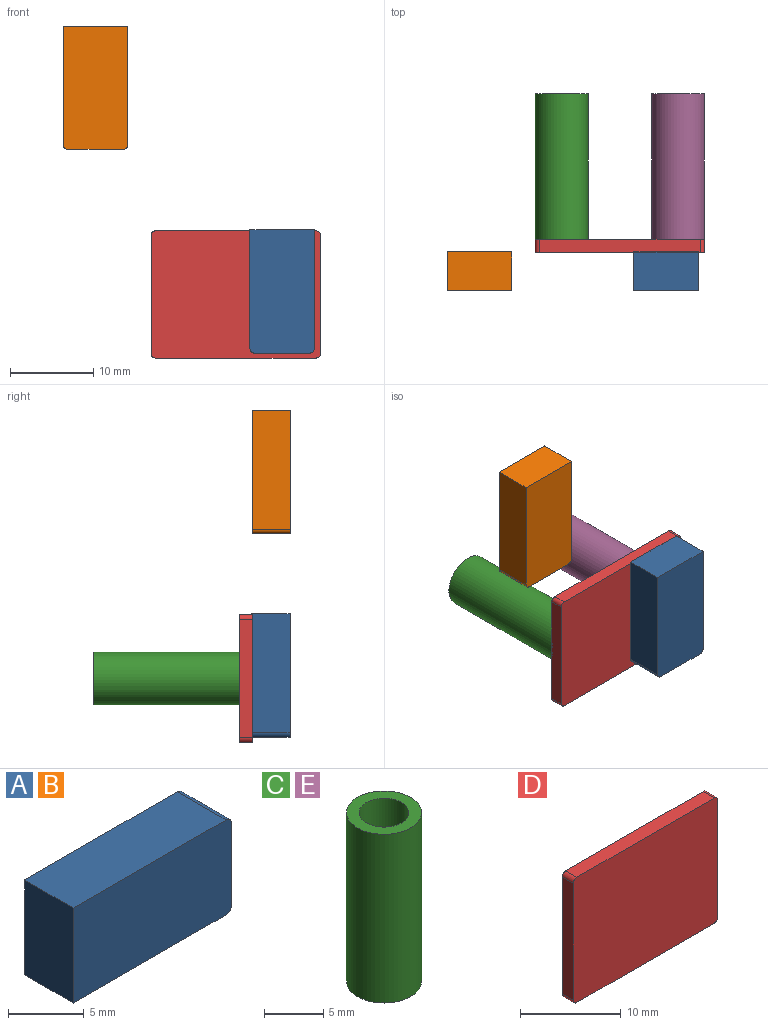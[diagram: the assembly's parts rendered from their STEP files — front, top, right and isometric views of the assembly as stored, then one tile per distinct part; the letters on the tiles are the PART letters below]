
ASSEMBLY  parts=5 mates=3
PART A: 8 faces, bbox 14.8x4.6x7.7 mm
  f0: plane 14.3x4.57mm, normal (0,0,1), area 65.4mm2, adj f1,f4,f5,f6
  f1: plane 7.7x4.57mm, normal (-1,0,0), area 35.2mm2, adj f0,f2,f4,f5
  f2: plane 14.3x4.57mm, normal (0,0,-1), area 65.4mm2, adj f1,f4,f5,f7
  f3: plane 6.68x4.57mm, normal (1,0,0), area 30.5mm2, adj f4,f5,f6,f7
  f4: plane 14.81x7.7mm, normal (0,-1,0), area 113.9mm2, adj f0,f1,f2,f3,f6,f7
  f5: plane 14.81x7.7mm, normal (0,1,0), area 113.9mm2, adj f0,f1,f2,f3,f6,f7
  f6: cylinder r=0.51mm len=4.57mm, axis (0,1,0), area 3.6mm2, adj f0,f3,f4,f5
  f7: cylinder r=0.51mm len=4.57mm, axis (0,-1,0), area 3.6mm2, adj f2,f3,f4,f5
PART B: same geometry as A
PART C: 4 faces, bbox 6.4x6.4x17.5 mm
  f0: cylinder r=2.11mm len=17.46mm, axis (0,0,-1), area 231.3mm2, adj f2,f3
  f1: cylinder r=3.17mm len=17.46mm, axis (0,0,-1), area 348.4mm2, adj f2,f3
  f2: plane 6.35x6.35mm, normal (0,0,1), area 17.7mm2, adj f0,f1
  f3: plane 6.35x6.35mm, normal (0,0,-1), area 17.7mm2, adj f0,f1
PART D: 10 faces, bbox 20.3x1.6x15.2 mm
  f0: plane 14.22x1.57mm, normal (1,0,0), area 22.4mm2, adj f4,f5,f6,f9
  f1: plane 19.3x1.57mm, normal (0,0,1), area 30.4mm2, adj f4,f5,f6,f7
  f2: plane 14.22x1.57mm, normal (-1,0,0), area 22.4mm2, adj f4,f5,f7,f8
  f3: plane 19.3x1.57mm, normal (0,0,-1), area 30.4mm2, adj f4,f5,f8,f9
  f4: plane 20.32x15.24mm, normal (0,-1,0), area 309.5mm2, adj f0,f1,f2,f3,f6,f7,f8,f9
  f5: plane 20.32x15.24mm, normal (0,1,0), area 309.5mm2, adj f0,f1,f2,f3,f6,f7,f8,f9
  f6: cylinder r=0.51mm len=1.57mm, axis (0,-1,0), area 1.3mm2, adj f0,f1,f4,f5
  f7: cylinder r=0.51mm len=1.57mm, axis (0,1,0), area 1.3mm2, adj f1,f2,f4,f5
  f8: cylinder r=0.51mm len=1.57mm, axis (0,-1,0), area 1.3mm2, adj f2,f3,f4,f5
  f9: cylinder r=0.51mm len=1.57mm, axis (0,1,0), area 1.3mm2, adj f0,f3,f4,f5
PART E: same geometry as C
PLACE A rot(axis=(0,1,0),90deg) t=(5.55,-1.53,0.38)mm
PLACE B rot(axis=(0,1,0),90deg) t=(-16.82,-1.57,24.8)mm
PLACE C rot(axis=(-1,0,0),90deg) t=(-6.99,8.73,0)mm
PLACE D at identity fixed
PLACE E rot(axis=(-1,0,0),90deg) t=(6.98,8.73,0)mm
MATE slider C.f0 <-> D.f5  axis (0,-1,0) through (-6.99,0,0)mm
MATE planar B.f5 <-> D.f4  axis (0,1,0) through (-16.82,-1.57,24.8)mm
MATE slider E.f0 <-> D.f5  axis (0,-1,0) through (6.98,0,0)mm
